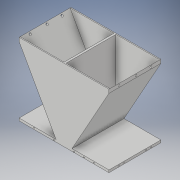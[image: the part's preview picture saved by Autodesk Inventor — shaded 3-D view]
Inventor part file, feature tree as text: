
AUTODESK INVENTOR PART (.ipt)
format: ipt  version: 2019 (Build 230136000, 136)  size: 271,872 bytes
history: native  units: in
note: dims shown in document units (in); Inventor stores cm internally (conversion verified against a paired STEP export)
features: extrude x22, sketch x22, fillet x4
ambient origin geometry x8: Origin, YZ Plane, XZ Plane, XY Plane, X Axis, Y Axis, Z Axis, Center Point
bodies: Solid1 (feature_tree)
feature tree (48):
  extrude  "Extrusion1"  Depth=0.1969in TaperAngle=0.0deg
  extrude  "Extrusion2"  Depth=0.0787in
  extrude  "Extrusion3"  Depth=0.0787in
  fillet  "Fillet1"  Radius=0.0787in
  fillet  "Fillet2"  Radius=4.9213in
  fillet  "Fillet3"  Radius=0.3937in
  fillet  "Fillet4"  Radius=0.3937in
  extrude  "Extrusion4"  Depth=0.3937in TaperAngle=0.0deg
  extrude  "Extrusion5"  Depth=0.3937in TaperAngle=0.0deg
  extrude  "Extrusion6"  Depth=0.4724in TaperAngle=0.0deg
  extrude  "Extrusion7"  Depth=0.4724in TaperAngle=0.0deg
  extrude  "Extrusion8"  Depth=0.9843in TaperAngle=0.0deg
  extrude  "Extrusion9"  Depth=0.9843in TaperAngle=0.0deg
  extrude  "Extrusion10"  Depth=0.9843in TaperAngle=0.0deg
  extrude  "Extrusion11"  Depth=0.9843in
  extrude  "Extrusion12"  Depth=0.9843in TaperAngle=0.0deg
  extrude  "Extrusion13"  Depth=0.9843in TaperAngle=0.0deg
  extrude  "Extrusion14"  [1 undecoded]
  extrude  "Extrusion15"  [1 undecoded]
  extrude  "Extrusion16"  [1 undecoded]
  extrude  "Extrusion17"  [1 undecoded]
  extrude  "Extrusion18"  [1 undecoded]
  extrude  "Extrusion19"  [1 undecoded]
  extrude  "Extrusion20"  [1 undecoded]
  extrude  "Extrusion21"  [1 undecoded]
  extrude  "Extrusion22"  [1 undecoded]
  sketch  "Sketch1"  dims[d10=9.8425in d11=0.0in d12=0.1969in d13=0.0in]
  sketch  "Sketch2"  dims[d14=0.1969in d15=0.0in d16=0.0787in]
  sketch  "Sketch3"  dims[d17=0.0787in d18=0.0787in d19=0.0787in d20=4.9213in d21=0.3937in d22=0.3937in d23=0.0in]
  sketch  "Sketch4"  dims[d32=0.3937in d33=0.0in d38=0.3937in d39=0.0in]
  sketch  "Sketch5"  dims[d40=0.3543in d41=0.3937in d42=0.0in]
  sketch  "Sketch6"  dims[d43=0.3937in d44=0.0in d45=0.4724in d46=0.0in]
  sketch  "Sketch7"  dims[d47=0.4724in d48=0.0in d49=0.4724in d50=0.0in]
  sketch  "Sketch8"  dims[d53=0.3937in d54=0.0in d56=0.9843in d57=0.0in]
  sketch  "Sketch9"  dims[d58=0.9843in d59=0.0in d60=0.9843in d61=0.0in]
  sketch  "Sketch10"  dims[d72=0.9843in d73=0.0in d79=0.9843in d80=0.0in]
  sketch  "Sketch11"  dims[d83=0.9843in d84=0.0in d85=3.937in]
  sketch  "Sketch12"  dims[d86=0.1969in d87=0.9843in d88=0.0in]
  sketch  "Sketch13"  dims[d94=0.9843in d95=0.0in d100=0.9843in d101=0.0in]
  sketch  "Sketch14"  dims[d108=0.9843in d109=0.0in]
  sketch  "Sketch15"
  sketch  "Sketch16"
  sketch  "Sketch17"
  sketch  "Sketch18"
  sketch  "Sketch19"
  sketch  "Sketch20"
  sketch  "Sketch21"
  sketch  "Sketch22"
note: 9 required parameter values undecoded (feature->parameter linkage not recoverable at this tier; creation-order binding heuristic only, values carry confidence <= 0.55)
